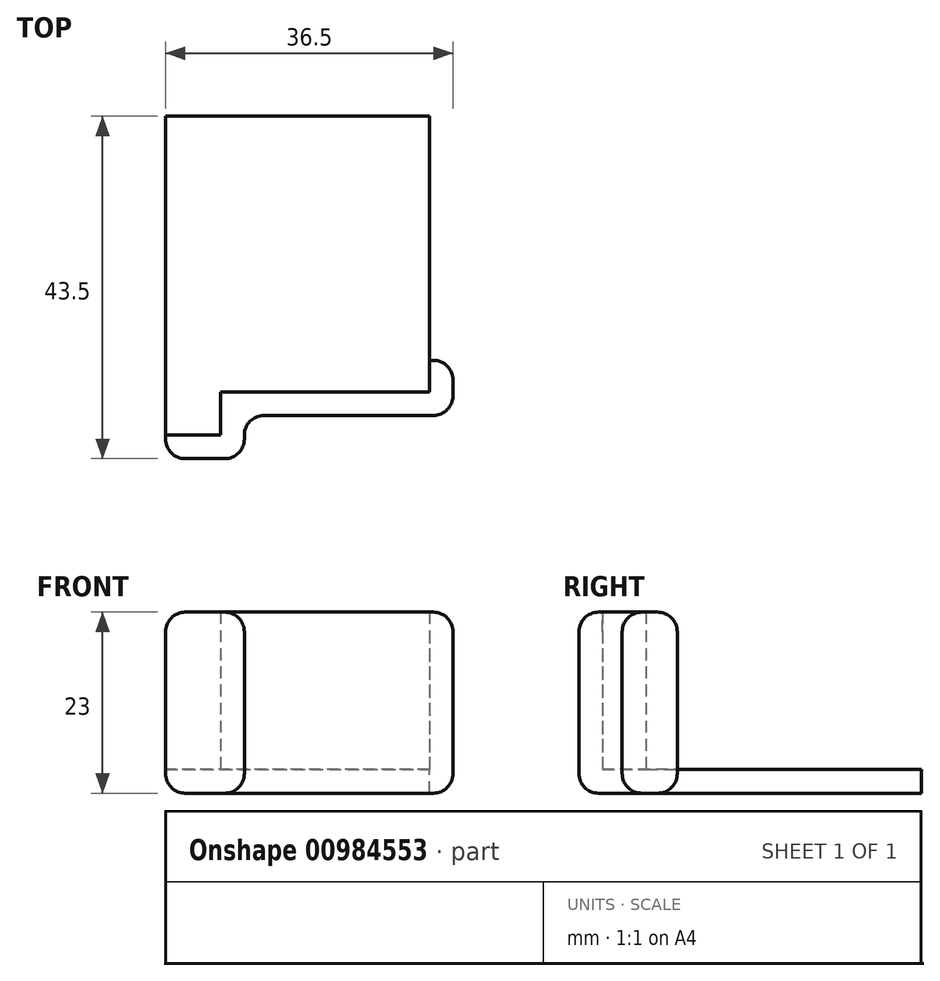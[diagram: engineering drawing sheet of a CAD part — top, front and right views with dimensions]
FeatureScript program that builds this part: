
annotation { "Feature Type Name" : "Feature", "Feature Type Description" : "" }
export const myFeature = defineFeature(function(context is Context, id is Id, definition is map)
    precondition{}
    {
        {
            var Q0;
            Q0=qCreatedBy(makeId("Top.planeOp"),FACE);
            var sketch = newSketch(context, id + "F0", { "sketchPlane" : qUnion([Q0])});
            skLineSegment(sketch, "E0", {"start": v(-14.5, -15.63) * mm, "end": v(-7.5, -15.63) * mm});
            skLineSegment(sketch, "E1", {"start": v(-7.5, -15.63) * mm, "end": v(-7.5, -10.13) * mm});
            skLineSegment(sketch, "E2", {"start": v(-7.5, -10.13) * mm, "end": v(19, -10.13) * mm});
            skLineSegment(sketch, "E3", {"start": v(19, -10.13) * mm, "end": v(19, 24.87) * mm});
            skLineSegment(sketch, "E4", {"start": v(19, 24.88) * mm, "end": v(-14.5, 24.87) * mm});
            skLineSegment(sketch, "E5", {"start": v(-14.5, 24.87) * mm, "end": v(-14.5, -15.63) * mm});
            skLineSegment(sketch, "E6", {"start": v(-17.5, 24.87) * mm, "end": v(-17.5, -15.63) * mm});
            skLineSegment(sketch, "E7", {"start": v(-17.5, -15.63) * mm, "end": v(-17.5, -18.63) * mm});
            skLineSegment(sketch, "E8", {"start": v(-17.5, -18.63) * mm, "end": v(-7.5, -18.63) * mm});
            skLineSegment(sketch, "E9", {"start": v(-7.5, -18.63) * mm, "end": v(-4.5, -18.63) * mm});
            skLineSegment(sketch, "E10", {"start": v(-17.5, 24.87) * mm, "end": v(-17.5, 27.88) * mm});
            skLineSegment(sketch, "E11", {"start": v(-17.5, 27.88) * mm, "end": v(19, 27.88) * mm});
            skLineSegment(sketch, "E12", {"start": v(19, 27.88) * mm, "end": v(22, 27.88) * mm});
            skLineSegment(sketch, "E13", {"start": v(22, 27.88) * mm, "end": v(22, -10.13) * mm});
            skLineSegment(sketch, "E14", {"start": v(22, -10.12) * mm, "end": v(22, -13.13) * mm});
            skLineSegment(sketch, "E15", {"start": v(22, -13.13) * mm, "end": v(-4.5, -13.13) * mm});
            skLineSegment(sketch, "E16", {"start": v(-4.5, -13.13) * mm, "end": v(-4.5, -18.63) * mm});
            skLineSegment(sketch, "E17", {"start": v(19, -10.13) * mm, "end": v(19, -13.13) * mm});
            skLineSegment(sketch, "E18", {"start": v(19, -13.13) * mm, "end": v(19, 27.88) * mm});
            skLineSegment(sketch, "E19", {"start": v(-4.5, -13.13) * mm, "end": v(-4.5, -10.13) * mm});
            skLineSegment(sketch, "E20", {"start": v(-14.5, -15.63) * mm, "end": v(-14.5, -18.63) * mm});
            skLineSegment(sketch, "E21", {"start": v(-14.5, -15.63) * mm, "end": v(-17.5, -15.63) * mm});
            skLineSegment(sketch, "E22", {"start": v(19, 24.87) * mm, "end": v(22, 24.87) * mm});
            skLineSegment(sketch, "E23", {"start": v(-14.5, 24.87) * mm, "end": v(-17.5, 24.87) * mm});
            skLineSegment(sketch, "E24", {"start": v(22, -13.13) * mm, "end": v(22, -6.13) * mm});
            skLineSegment(sketch, "E25", {"start": v(22, -6.13) * mm, "end": v(19, -6.13) * mm});
            skSolve(sketch);
        }
        {
            var Q0;
            Q0=makeQuery(id+"F0.imprint","IMPRINT",FACE,{"disambiguationData":[TD([[makeQuery(id+"F0.imprint","IMPRINT",EDGE,{"derivedFrom":sQuery(id+"F0.wireOp",EDGE,"E0")}),1.0]])]});
            var Q1;
            Q1=makeQuery(id+"F0.imprint","IMPRINT",FACE,{"disambiguationData":[TD([[makeQuery(id+"F0.imprint","IMPRINT",EDGE,{"derivedFrom":sQuery(id+"F0.wireOp",EDGE,"E0")}),-1.0]])]});
            var Q2;
            {var subQ3=sQuery(id+"F0.wireOp",EDGE,"E19");Q2=makeQuery(id+"F0.imprint","IMPRINT",FACE,{"disambiguationData":[TD([[makeQuery(id+"F0.imprint","IMPRINT",EDGE,{"derivedFrom":subQ3}),-1.0]])]});}
            var Q3;
            {var subQ1=sQuery(id+"F0.wireOp",EDGE,"E14");Q3=makeQuery(id+"F0.imprint","IMPRINT",FACE,{"disambiguationData":[TD([[makeQuery(id+"F0.imprint","IMPRINT",EDGE,{"derivedFrom":subQ1}),-1.0]])]});}
            var Q4;
            {var subQ0=sQuery(id+"F0.wireOp",EDGE,"E24");Q4=makeQuery(id+"F0.imprint","IMPRINT",FACE,{"disambiguationData":[TD([[makeQuery(id+"F0.imprint","IMPRINT",EDGE,{"derivedFrom":subQ0}),1.0]])]});}
            extrude(context, id + "F1", {"entities" : qUnion([Q0, Q1, Q2, Q3, Q4]), "oppositeDirection" : true, "depth" : 3 * mm, "offsetDistance" : 25 * mm});
        }
        {
            var Q0;
            {var subQ1=sQuery(id+"F0.wireOp",EDGE,"E14");Q0=makeQuery(id+"F0.imprint","IMPRINT",FACE,{"disambiguationData":[TD([[makeQuery(id+"F0.imprint","IMPRINT",EDGE,{"derivedFrom":subQ1}),-1.0]])]});}
            var Q1;
            {var subQ3=sQuery(id+"F0.wireOp",EDGE,"E19");Q1=makeQuery(id+"F0.imprint","IMPRINT",FACE,{"disambiguationData":[TD([[makeQuery(id+"F0.imprint","IMPRINT",EDGE,{"derivedFrom":subQ3}),-1.0]])]});}
            var Q2;
            Q2=makeQuery(id+"F0.imprint","IMPRINT",FACE,{"disambiguationData":[TD([[makeQuery(id+"F0.imprint","IMPRINT",EDGE,{"derivedFrom":sQuery(id+"F0.wireOp",EDGE,"E0")}),-1.0]])]});
            var Q3;
            {var subQ0=sQuery(id+"F0.wireOp",EDGE,"E24");Q3=makeQuery(id+"F0.imprint","IMPRINT",FACE,{"disambiguationData":[TD([[makeQuery(id+"F0.imprint","IMPRINT",EDGE,{"derivedFrom":subQ0}),1.0]])]});}
            extrude(context, id + "F2", {"entities" : qUnion([Q0, Q1, Q2, Q3]), "operationType" : NewBodyOperationType.ADD, "depth" : 20 * mm, "offsetDistance" : 25 * mm});
        }
        {
            var Q0;
            Q0=makeQuery(id+"F1.opExtrude","CAP_EDGE",EDGE,{"disambiguationData":[OSD([sQuery(id+"F0.wireOp",EDGE,"E5"),sQuery(id+"F0.wireOp",EDGE,"E20")])],"isStart":false});
            var Q1;
            {var subQ0=sQuery(id+"F0.wireOp",EDGE,"E20");var subQ1=sQuery(id+"F0.wireOp",EDGE,"E8");Q1=makeQuery(id+"F2.boolean.opBoolean","MERGE",EDGE,{"derivedFrom":[makeQuery(id+"F1.opExtrude","SWEPT_EDGE",EDGE,{"disambiguationData":[OSD([subQ1,subQ0])]}),makeQuery(id+"F2.opExtrude","SWEPT_EDGE",EDGE,{"disambiguationData":[OSD([subQ1,subQ0])]})]});}
            var Q2;
            Q2=makeQuery(id+"F1.opExtrude","CAP_EDGE",EDGE,{"disambiguationData":[OSD([sQuery(id+"F0.wireOp",EDGE,"E8"),sQuery(id+"F0.wireOp",EDGE,"E9")])],"isStart":false});
            var Q3;
            Q3=makeQuery(id+"F1.opExtrude","CAP_EDGE",EDGE,{"disambiguationData":[OSD([sQuery(id+"F0.wireOp",EDGE,"E16")])],"isStart":false});
            var Q4;
            Q4=makeQuery(id+"F1.opExtrude","CAP_EDGE",EDGE,{"disambiguationData":[OSD([sQuery(id+"F0.wireOp",EDGE,"E15")])],"isStart":false});
            var Q5;
            {var subQ0=sQuery(id+"F0.wireOp",EDGE,"E19");var subQ1=sQuery(id+"F0.wireOp",EDGE,"E16");var subQ2=sQuery(id+"F0.wireOp",EDGE,"E15");Q5=makeQuery(id+"F2.boolean.opBoolean","MERGE",EDGE,{"derivedFrom":[makeQuery(id+"F1.opExtrude","SWEPT_EDGE",EDGE,{"disambiguationData":[OSD([subQ2,subQ1,subQ0])]}),makeQuery(id+"F2.opExtrude","SWEPT_EDGE",EDGE,{"disambiguationData":[OSD([subQ2,subQ1,subQ0])]})]});}
            var Q6;
            {var subQ0=sQuery(id+"F0.wireOp",EDGE,"E16");var subQ1=sQuery(id+"F0.wireOp",EDGE,"E9");Q6=makeQuery(id+"F2.boolean.opBoolean","MERGE",EDGE,{"derivedFrom":[makeQuery(id+"F1.opExtrude","SWEPT_EDGE",EDGE,{"disambiguationData":[OSD([subQ1,subQ0])]}),makeQuery(id+"F2.opExtrude","SWEPT_EDGE",EDGE,{"disambiguationData":[OSD([subQ1,subQ0])]})]});}
            var Q7;
            {var subQ0=sQuery(id+"F0.wireOp",EDGE,"E15");var subQ1=sQuery(id+"F0.wireOp",EDGE,"E14");Q7=makeQuery(id+"F2.boolean.opBoolean","MERGE",EDGE,{"derivedFrom":[makeQuery(id+"F1.opExtrude","SWEPT_EDGE",EDGE,{"disambiguationData":[OSD([subQ1,subQ0])]}),makeQuery(id+"F2.opExtrude","SWEPT_EDGE",EDGE,{"disambiguationData":[OSD([subQ1,subQ0])]})]});}
            var Q8;
            Q8=makeQuery(id+"F1.opExtrude","CAP_EDGE",EDGE,{"disambiguationData":[OSD([sQuery(id+"F0.wireOp",EDGE,"E13"),sQuery(id+"F0.wireOp",EDGE,"E14")])],"isStart":false});
            var Q9;
            Q9=makeQuery(id+"F2.opExtrude","CAP_EDGE",EDGE,{"disambiguationData":[OSD([sQuery(id+"F0.wireOp",EDGE,"E15")])],"isStart":false});
            var Q10;
            Q10=makeQuery(id+"F2.opExtrude","CAP_EDGE",EDGE,{"disambiguationData":[OSD([sQuery(id+"F0.wireOp",EDGE,"E16")])],"isStart":false});
            var Q11;
            Q11=makeQuery(id+"F2.opExtrude","CAP_EDGE",EDGE,{"disambiguationData":[OSD([sQuery(id+"F0.wireOp",EDGE,"E8"),sQuery(id+"F0.wireOp",EDGE,"E9")])],"isStart":false});
            var Q12;
            Q12=makeQuery(id+"F2.opExtrude","CAP_EDGE",EDGE,{"disambiguationData":[OSD([sQuery(id+"F0.wireOp",EDGE,"E13"),sQuery(id+"F0.wireOp",EDGE,"E14")])],"isStart":false});
            var Q13;
            Q13=makeQuery(id+"F2.opExtrude","CAP_EDGE",EDGE,{"disambiguationData":[OSD([sQuery(id+"F0.wireOp",EDGE,"E24")])],"isStart":false});
            var Q14;
            Q14=makeQuery(id+"F1.opExtrude","CAP_EDGE",EDGE,{"disambiguationData":[OSD([sQuery(id+"F0.wireOp",EDGE,"E24")])],"isStart":false});
            var Q15;
            {var subQ0=sQuery(id+"F0.wireOp",EDGE,"E25");var subQ1=sQuery(id+"F0.wireOp",EDGE,"E24");var subQ2=sQuery(id+"F0.wireOp",EDGE,"E13");Q15=makeQuery(id+"F2.boolean.opBoolean","MERGE",EDGE,{"derivedFrom":[makeQuery(id+"F1.opExtrude","SWEPT_EDGE",EDGE,{"disambiguationData":[OSD([subQ2,subQ1,subQ0])]}),makeQuery(id+"F2.opExtrude","SWEPT_EDGE",EDGE,{"disambiguationData":[OSD([subQ2,subQ1,subQ0])]})]});}
            var Q16;
            Q16=makeQuery(id+"F1.opExtrude","CAP_EDGE",EDGE,{"disambiguationData":[OSD([sQuery(id+"F0.wireOp",EDGE,"E25")])],"isStart":false});
            var Q17;
            Q17=makeQuery(id+"F1.opExtrude","CAP_EDGE",EDGE,{"disambiguationData":[OSD([sQuery(id+"F0.wireOp",EDGE,"E18")])],"isStart":false});
            var Q18;
            Q18=makeQuery(id+"F2.opExtrude","CAP_EDGE",EDGE,{"disambiguationData":[OSD([sQuery(id+"F0.wireOp",EDGE,"E25")])],"isStart":false});
            var Q19;
            Q19=makeQuery(id+"F2.opExtrude","CAP_EDGE",EDGE,{"disambiguationData":[OSD([sQuery(id+"F0.wireOp",EDGE,"E20")])],"isStart":false});
            fillet(context, id + "F3", {"entities" : qUnion([Q0, Q1, Q2, Q3, Q4, Q5, Q6, Q7, Q8, Q9, Q10, Q11, Q12, Q13, Q14, Q15, Q16, Q17, Q18, Q19]), "radius" : 2.5 * mm, "tangentPropagation" : true, "allowEdgeOverflow" : false});
        }
    });
